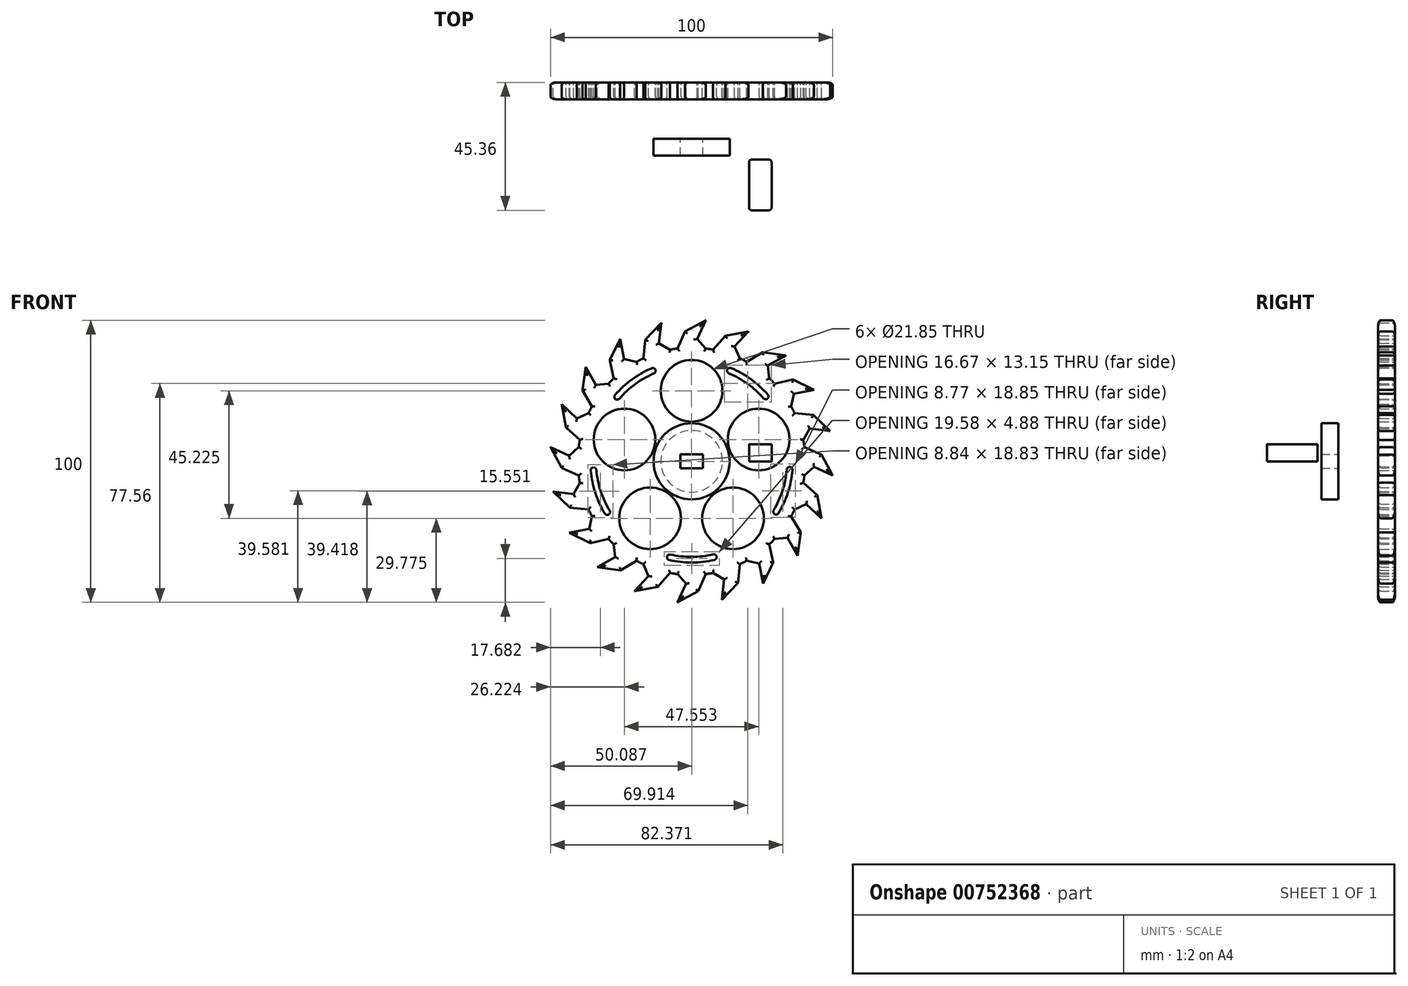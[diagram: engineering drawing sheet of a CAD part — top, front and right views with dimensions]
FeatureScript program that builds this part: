
annotation { "Feature Type Name" : "Feature", "Feature Type Description" : "" }
export const myFeature = defineFeature(function(context is Context, id is Id, definition is map)
    precondition{}
    {
        {
            var Q0;
            Q0=qCreatedBy(makeId("Front.planeOp"),FACE);
            var sketch = newSketch(context, id + "F0", { "sketchPlane" : qUnion([Q0])});
            skCircle(sketch, "E0", {"center": v(0, 0) * mm, "radius": 10.93 * mm});
            skLineSegment(sketch, "E1", {"start": v(0, 0) * mm, "end": v(0, 25) * mm, "construction": true});
            skCircle(sketch, "E2", {"center": v(0, 25) * mm, "radius": 10.43 * mm});
            skCircle(sketch, "E3.1.0", {"center": v(-23.78, 7.73) * mm, "radius": 10.43 * mm});
            skCircle(sketch, "E3.2.0", {"center": v(-14.7, -20.23) * mm, "radius": 10.43 * mm});
            skCircle(sketch, "E3.3.0", {"center": v(14.7, -20.23) * mm, "radius": 10.43 * mm});
            skCircle(sketch, "E3.4.0", {"center": v(23.78, 7.73) * mm, "radius": 10.43 * mm});
            skLineSegment(sketch, "E4.bottom", {"start": v(5, 40) * mm, "end": v(-5, 40) * mm, "construction": true});
            skPoint(sketch, "E4.middle", {"position": v(0, 45) * mm});
            skLineSegment(sketch, "E5", {"start": v(-5, 40) * mm, "end": v(-2.33, 46.08) * mm});
            skLineSegment(sketch, "E6", {"start": v(-2.33, 46.08) * mm, "end": v(5, 50) * mm});
            skLineSegment(sketch, "E7", {"start": v(5, 50) * mm, "end": v(1.93, 43.37) * mm});
            skLineSegment(sketch, "E8", {"start": v(1.93, 43.37) * mm, "end": v(5, 40) * mm});
            skLineSegment(sketch, "E9.1.0", {"start": v(-16.45, 43.1) * mm, "end": v(-10.7, 49.1) * mm});
            skLineSegment(sketch, "E9.1.1", {"start": v(-17.12, 36.5) * mm, "end": v(-16.45, 43.1) * mm});
            skLineSegment(sketch, "E9.1.2", {"start": v(-10.7, 49.1) * mm, "end": v(-11.57, 41.85) * mm});
            skPoint(sketch, "E9.1.3", {"position": v(-13.9, 42.8) * mm});
            skLineSegment(sketch, "E9.1.4", {"start": v(-7.6, 39.59) * mm, "end": v(-17.12, 36.5) * mm, "construction": true});
            skLineSegment(sketch, "E9.1.5", {"start": v(-11.57, 41.85) * mm, "end": v(-7.6, 39.59) * mm});
            skLineSegment(sketch, "E9.2.0", {"start": v(-28.97, 35.91) * mm, "end": v(-25.34, 43.39) * mm});
            skLineSegment(sketch, "E9.2.1", {"start": v(-27.56, 29.42) * mm, "end": v(-28.97, 35.91) * mm});
            skLineSegment(sketch, "E9.2.2", {"start": v(-25.34, 43.39) * mm, "end": v(-23.93, 36.22) * mm});
            skPoint(sketch, "E9.2.3", {"position": v(-26.45, 36.4) * mm});
            skLineSegment(sketch, "E9.2.4", {"start": v(-19.47, 35.3) * mm, "end": v(-27.56, 29.42) * mm, "construction": true});
            skLineSegment(sketch, "E9.2.5", {"start": v(-23.93, 36.22) * mm, "end": v(-19.47, 35.3) * mm});
            skLineSegment(sketch, "E9.3.0", {"start": v(-38.65, 25.2) * mm, "end": v(-37.51, 33.43) * mm});
            skLineSegment(sketch, "E9.3.1", {"start": v(-35.3, 19.47) * mm, "end": v(-38.65, 25.2) * mm});
            skLineSegment(sketch, "E9.3.2", {"start": v(-37.51, 33.43) * mm, "end": v(-33.96, 27.06) * mm});
            skPoint(sketch, "E9.3.3", {"position": v(-36.4, 26.45) * mm});
            skLineSegment(sketch, "E9.3.4", {"start": v(-29.42, 27.56) * mm, "end": v(-35.3, 19.47) * mm, "construction": true});
            skLineSegment(sketch, "E9.3.5", {"start": v(-33.96, 27.06) * mm, "end": v(-29.42, 27.56) * mm});
            skLineSegment(sketch, "E9.4.0", {"start": v(-44.54, 12.03) * mm, "end": v(-46, 20.2) * mm});
            skLineSegment(sketch, "E9.4.1", {"start": v(-39.59, 7.6) * mm, "end": v(-44.54, 12.03) * mm});
            skLineSegment(sketch, "E9.4.2", {"start": v(-46, 20.2) * mm, "end": v(-40.66, 15.24) * mm});
            skPoint(sketch, "E9.4.3", {"position": v(-42.8, 13.9) * mm});
            skLineSegment(sketch, "E9.4.4", {"start": v(-36.5, 17.12) * mm, "end": v(-39.59, 7.6) * mm, "construction": true});
            skLineSegment(sketch, "E9.4.5", {"start": v(-40.66, 15.24) * mm, "end": v(-36.5, 17.12) * mm});
            skLineSegment(sketch, "E9.5.0", {"start": v(-46.08, -2.33) * mm, "end": v(-50, 5) * mm});
            skLineSegment(sketch, "E9.5.1", {"start": v(-40, -5) * mm, "end": v(-46.08, -2.33) * mm});
            skLineSegment(sketch, "E9.5.2", {"start": v(-50, 5) * mm, "end": v(-43.37, 1.93) * mm});
            skPoint(sketch, "E9.5.3", {"position": v(-45, 0) * mm});
            skLineSegment(sketch, "E9.5.4", {"start": v(-40, 5) * mm, "end": v(-40, -5) * mm, "construction": true});
            skLineSegment(sketch, "E9.5.5", {"start": v(-43.37, 1.93) * mm, "end": v(-40, 5) * mm});
            skLineSegment(sketch, "E9.6.0", {"start": v(-43.1, -16.45) * mm, "end": v(-49.1, -10.7) * mm});
            skLineSegment(sketch, "E9.6.1", {"start": v(-36.5, -17.12) * mm, "end": v(-43.1, -16.45) * mm});
            skLineSegment(sketch, "E9.6.2", {"start": v(-49.1, -10.7) * mm, "end": v(-41.85, -11.57) * mm});
            skPoint(sketch, "E9.6.3", {"position": v(-42.8, -13.9) * mm});
            skLineSegment(sketch, "E9.6.4", {"start": v(-39.59, -7.6) * mm, "end": v(-36.5, -17.12) * mm, "construction": true});
            skLineSegment(sketch, "E9.6.5", {"start": v(-41.85, -11.57) * mm, "end": v(-39.59, -7.6) * mm});
            skLineSegment(sketch, "E9.7.0", {"start": v(-35.91, -28.97) * mm, "end": v(-43.39, -25.34) * mm});
            skLineSegment(sketch, "E9.7.1", {"start": v(-29.42, -27.56) * mm, "end": v(-35.91, -28.97) * mm});
            skLineSegment(sketch, "E9.7.2", {"start": v(-43.39, -25.34) * mm, "end": v(-36.22, -23.93) * mm});
            skPoint(sketch, "E9.7.3", {"position": v(-36.4, -26.45) * mm});
            skLineSegment(sketch, "E9.7.4", {"start": v(-35.3, -19.47) * mm, "end": v(-29.42, -27.56) * mm, "construction": true});
            skLineSegment(sketch, "E9.7.5", {"start": v(-36.22, -23.93) * mm, "end": v(-35.3, -19.47) * mm});
            skLineSegment(sketch, "E9.8.0", {"start": v(-25.2, -38.65) * mm, "end": v(-33.43, -37.51) * mm});
            skLineSegment(sketch, "E9.8.1", {"start": v(-19.47, -35.3) * mm, "end": v(-25.2, -38.65) * mm});
            skLineSegment(sketch, "E9.8.2", {"start": v(-33.43, -37.51) * mm, "end": v(-27.06, -33.96) * mm});
            skPoint(sketch, "E9.8.3", {"position": v(-26.45, -36.4) * mm});
            skLineSegment(sketch, "E9.8.4", {"start": v(-27.56, -29.42) * mm, "end": v(-19.47, -35.3) * mm, "construction": true});
            skLineSegment(sketch, "E9.8.5", {"start": v(-27.06, -33.96) * mm, "end": v(-27.56, -29.42) * mm});
            skLineSegment(sketch, "E9.9.0", {"start": v(-12.03, -44.54) * mm, "end": v(-20.2, -46) * mm});
            skLineSegment(sketch, "E9.9.1", {"start": v(-7.6, -39.59) * mm, "end": v(-12.03, -44.54) * mm});
            skLineSegment(sketch, "E9.9.2", {"start": v(-20.2, -46) * mm, "end": v(-15.24, -40.66) * mm});
            skPoint(sketch, "E9.9.3", {"position": v(-13.9, -42.8) * mm});
            skLineSegment(sketch, "E9.9.4", {"start": v(-17.12, -36.5) * mm, "end": v(-7.6, -39.59) * mm, "construction": true});
            skLineSegment(sketch, "E9.9.5", {"start": v(-15.24, -40.66) * mm, "end": v(-17.12, -36.5) * mm});
            skLineSegment(sketch, "E9.10.0", {"start": v(2.33, -46.08) * mm, "end": v(-5, -50) * mm});
            skLineSegment(sketch, "E9.10.1", {"start": v(5, -40) * mm, "end": v(2.33, -46.08) * mm});
            skLineSegment(sketch, "E9.10.2", {"start": v(-5, -50) * mm, "end": v(-1.93, -43.37) * mm});
            skPoint(sketch, "E9.10.3", {"position": v(0, -45) * mm});
            skLineSegment(sketch, "E9.10.4", {"start": v(-5, -40) * mm, "end": v(5, -40) * mm, "construction": true});
            skLineSegment(sketch, "E9.10.5", {"start": v(-1.93, -43.37) * mm, "end": v(-5, -40) * mm});
            skLineSegment(sketch, "E9.11.0", {"start": v(16.45, -43.1) * mm, "end": v(10.7, -49.1) * mm});
            skLineSegment(sketch, "E9.11.1", {"start": v(17.12, -36.5) * mm, "end": v(16.45, -43.1) * mm});
            skLineSegment(sketch, "E9.11.2", {"start": v(10.7, -49.1) * mm, "end": v(11.57, -41.85) * mm});
            skPoint(sketch, "E9.11.3", {"position": v(13.9, -42.8) * mm});
            skLineSegment(sketch, "E9.11.4", {"start": v(7.6, -39.59) * mm, "end": v(17.12, -36.5) * mm, "construction": true});
            skLineSegment(sketch, "E9.11.5", {"start": v(11.57, -41.85) * mm, "end": v(7.6, -39.59) * mm});
            skLineSegment(sketch, "E9.12.0", {"start": v(28.97, -35.91) * mm, "end": v(25.34, -43.39) * mm});
            skLineSegment(sketch, "E9.12.1", {"start": v(27.56, -29.42) * mm, "end": v(28.97, -35.91) * mm});
            skLineSegment(sketch, "E9.12.2", {"start": v(25.34, -43.39) * mm, "end": v(23.93, -36.22) * mm});
            skPoint(sketch, "E9.12.3", {"position": v(26.45, -36.4) * mm});
            skLineSegment(sketch, "E9.12.4", {"start": v(19.47, -35.3) * mm, "end": v(27.56, -29.42) * mm, "construction": true});
            skLineSegment(sketch, "E9.12.5", {"start": v(23.93, -36.22) * mm, "end": v(19.47, -35.3) * mm});
            skLineSegment(sketch, "E9.13.0", {"start": v(38.65, -25.2) * mm, "end": v(37.51, -33.43) * mm});
            skLineSegment(sketch, "E9.13.1", {"start": v(35.3, -19.47) * mm, "end": v(38.65, -25.2) * mm});
            skLineSegment(sketch, "E9.13.2", {"start": v(37.51, -33.43) * mm, "end": v(33.96, -27.06) * mm});
            skPoint(sketch, "E9.13.3", {"position": v(36.4, -26.45) * mm});
            skLineSegment(sketch, "E9.13.4", {"start": v(29.42, -27.56) * mm, "end": v(35.3, -19.47) * mm, "construction": true});
            skLineSegment(sketch, "E9.13.5", {"start": v(33.96, -27.06) * mm, "end": v(29.42, -27.56) * mm});
            skLineSegment(sketch, "E9.14.0", {"start": v(44.54, -12.03) * mm, "end": v(46, -20.2) * mm});
            skLineSegment(sketch, "E9.14.1", {"start": v(39.59, -7.6) * mm, "end": v(44.54, -12.03) * mm});
            skLineSegment(sketch, "E9.14.2", {"start": v(46, -20.2) * mm, "end": v(40.66, -15.24) * mm});
            skPoint(sketch, "E9.14.3", {"position": v(42.8, -13.9) * mm});
            skLineSegment(sketch, "E9.14.4", {"start": v(36.5, -17.12) * mm, "end": v(39.59, -7.6) * mm, "construction": true});
            skLineSegment(sketch, "E9.14.5", {"start": v(40.66, -15.24) * mm, "end": v(36.5, -17.12) * mm});
            skLineSegment(sketch, "E9.15.0", {"start": v(46.08, 2.33) * mm, "end": v(50, -5) * mm});
            skLineSegment(sketch, "E9.15.1", {"start": v(40, 5) * mm, "end": v(46.08, 2.33) * mm});
            skLineSegment(sketch, "E9.15.2", {"start": v(50, -5) * mm, "end": v(43.37, -1.93) * mm});
            skPoint(sketch, "E9.15.3", {"position": v(45, 0) * mm});
            skLineSegment(sketch, "E9.15.4", {"start": v(40, -5) * mm, "end": v(40, 5) * mm, "construction": true});
            skLineSegment(sketch, "E9.15.5", {"start": v(43.37, -1.93) * mm, "end": v(40, -5) * mm});
            skLineSegment(sketch, "E9.16.0", {"start": v(43.1, 16.45) * mm, "end": v(49.1, 10.7) * mm});
            skLineSegment(sketch, "E9.16.1", {"start": v(36.5, 17.12) * mm, "end": v(43.1, 16.45) * mm});
            skLineSegment(sketch, "E9.16.2", {"start": v(49.1, 10.7) * mm, "end": v(41.85, 11.57) * mm});
            skPoint(sketch, "E9.16.3", {"position": v(42.8, 13.9) * mm});
            skLineSegment(sketch, "E9.16.4", {"start": v(39.59, 7.6) * mm, "end": v(36.5, 17.12) * mm, "construction": true});
            skLineSegment(sketch, "E9.16.5", {"start": v(41.85, 11.57) * mm, "end": v(39.59, 7.6) * mm});
            skLineSegment(sketch, "E9.17.0", {"start": v(35.91, 28.97) * mm, "end": v(43.39, 25.34) * mm});
            skLineSegment(sketch, "E9.17.1", {"start": v(29.42, 27.56) * mm, "end": v(35.91, 28.97) * mm});
            skLineSegment(sketch, "E9.17.2", {"start": v(43.39, 25.34) * mm, "end": v(36.22, 23.93) * mm});
            skPoint(sketch, "E9.17.3", {"position": v(36.4, 26.45) * mm});
            skLineSegment(sketch, "E9.17.4", {"start": v(35.3, 19.47) * mm, "end": v(29.42, 27.56) * mm, "construction": true});
            skLineSegment(sketch, "E9.17.5", {"start": v(36.22, 23.93) * mm, "end": v(35.3, 19.47) * mm});
            skLineSegment(sketch, "E9.18.0", {"start": v(25.2, 38.65) * mm, "end": v(33.43, 37.51) * mm});
            skLineSegment(sketch, "E9.18.1", {"start": v(19.47, 35.3) * mm, "end": v(25.2, 38.65) * mm});
            skLineSegment(sketch, "E9.18.2", {"start": v(33.43, 37.51) * mm, "end": v(27.06, 33.96) * mm});
            skPoint(sketch, "E9.18.3", {"position": v(26.45, 36.4) * mm});
            skLineSegment(sketch, "E9.18.4", {"start": v(27.56, 29.42) * mm, "end": v(19.47, 35.3) * mm, "construction": true});
            skLineSegment(sketch, "E9.18.5", {"start": v(27.06, 33.96) * mm, "end": v(27.56, 29.42) * mm});
            skLineSegment(sketch, "E9.19.0", {"start": v(12.03, 44.54) * mm, "end": v(20.2, 46) * mm});
            skLineSegment(sketch, "E9.19.1", {"start": v(7.6, 39.59) * mm, "end": v(12.03, 44.54) * mm});
            skLineSegment(sketch, "E9.19.2", {"start": v(20.2, 46) * mm, "end": v(15.24, 40.66) * mm});
            skPoint(sketch, "E9.19.3", {"position": v(13.9, 42.8) * mm});
            skLineSegment(sketch, "E9.19.4", {"start": v(17.12, 36.5) * mm, "end": v(7.6, 39.59) * mm, "construction": true});
            skLineSegment(sketch, "E9.19.5", {"start": v(15.24, 40.66) * mm, "end": v(17.12, 36.5) * mm});
            skArc(sketch, "E10", {"start": v(-17.12, 36.5) * mm, "mid": v(-18.3, 35.92) * mm, "end": v(-19.47, 35.3) * mm});
            skArc(sketch, "E11.trimOffspring", {"start": v(-5, 40) * mm, "mid": v(-6.3, 39.81) * mm, "end": v(-7.6, 39.59) * mm});
            skArc(sketch, "E12.trimOffspring", {"start": v(7.6, 39.59) * mm, "mid": v(6.3, 39.81) * mm, "end": v(5, 40) * mm});
            skArc(sketch, "E13.trimOffspring", {"start": v(19.47, 35.3) * mm, "mid": v(18.3, 35.92) * mm, "end": v(17.12, 36.5) * mm});
            skArc(sketch, "E14.trimOffspring", {"start": v(29.42, 27.56) * mm, "mid": v(28.5, 28.5) * mm, "end": v(27.56, 29.42) * mm});
            skArc(sketch, "E15.trimOffspring", {"start": v(36.5, 17.12) * mm, "mid": v(35.92, 18.3) * mm, "end": v(35.3, 19.47) * mm});
            skArc(sketch, "E16.trimOffspring", {"start": v(40, 5) * mm, "mid": v(39.81, 6.3) * mm, "end": v(39.59, 7.6) * mm});
            skArc(sketch, "E17.trimOffspring", {"start": v(39.59, -7.6) * mm, "mid": v(39.81, -6.3) * mm, "end": v(40, -5) * mm});
            skArc(sketch, "E18.trimOffspring", {"start": v(35.3, -19.47) * mm, "mid": v(35.92, -18.3) * mm, "end": v(36.5, -17.12) * mm});
            skArc(sketch, "E19.trimOffspring", {"start": v(27.56, -29.42) * mm, "mid": v(28.5, -28.5) * mm, "end": v(29.42, -27.56) * mm});
            skArc(sketch, "E20.trimOffspring", {"start": v(17.12, -36.5) * mm, "mid": v(18.3, -35.92) * mm, "end": v(19.47, -35.3) * mm});
            skArc(sketch, "E21.trimOffspring", {"start": v(5, -40) * mm, "mid": v(6.3, -39.81) * mm, "end": v(7.6, -39.59) * mm});
            skArc(sketch, "E22.trimOffspring", {"start": v(-7.6, -39.59) * mm, "mid": v(-6.3, -39.81) * mm, "end": v(-5, -40) * mm});
            skArc(sketch, "E23.trimOffspring", {"start": v(-19.47, -35.3) * mm, "mid": v(-18.3, -35.92) * mm, "end": v(-17.12, -36.5) * mm});
            skArc(sketch, "E24.trimOffspring", {"start": v(-29.42, -27.56) * mm, "mid": v(-28.5, -28.5) * mm, "end": v(-27.56, -29.42) * mm});
            skArc(sketch, "E25.trimOffspring", {"start": v(-36.5, -17.12) * mm, "mid": v(-35.92, -18.3) * mm, "end": v(-35.3, -19.47) * mm});
            skArc(sketch, "E26.trimOffspring", {"start": v(-40, -5) * mm, "mid": v(-39.81, -6.3) * mm, "end": v(-39.59, -7.6) * mm});
            skArc(sketch, "E27.trimOffspring", {"start": v(-39.59, 7.6) * mm, "mid": v(-39.81, 6.3) * mm, "end": v(-40, 5) * mm});
            skArc(sketch, "E28.trimOffspring", {"start": v(-35.3, 19.47) * mm, "mid": v(-35.92, 18.3) * mm, "end": v(-36.5, 17.12) * mm});
            skArc(sketch, "E29.trimOffspring", {"start": v(-27.56, 29.42) * mm, "mid": v(-28.5, 28.5) * mm, "end": v(-29.42, 27.56) * mm});
            skArc(sketch, "E30.0", {"start": v(-13.74, 32.07) * mm, "mid": v(-20.58, 28.17) * mm, "end": v(-26.37, 22.85) * mm});
            skArc(sketch, "E31.0.startCap", {"start": v(-14.14, 32.99) * mm, "mid": v(-12.82, 32.46) * mm, "end": v(-13.35, 31.15) * mm});
            skArc(sketch, "E31.0.endCap", {"start": v(-25.61, 22.2) * mm, "mid": v(-27.02, 22.1) * mm, "end": v(-27.12, 23.5) * mm});
            skArc(sketch, "E31.0.left", {"start": v(-13.35, 31.15) * mm, "mid": v(-19.99, 27.37) * mm, "end": v(-25.61, 22.2) * mm});
            skArc(sketch, "E31.0.right", {"start": v(-14.14, 32.99) * mm, "mid": v(-21.17, 28.98) * mm, "end": v(-27.12, 23.5) * mm});
            skArc(sketch, "E32.1.0", {"start": v(-35.74, -3.25) * mm, "mid": v(-34.1, -11.18) * mm, "end": v(-30.73, -18.53) * mm});
            skArc(sketch, "E32.1.1", {"start": v(-29.02, -17.5) * mm, "mid": v(-29.36, -18.87) * mm, "end": v(-30.73, -18.53) * mm});
            skArc(sketch, "E32.1.2", {"start": v(-35.74, -3.25) * mm, "mid": v(-34.84, -2.16) * mm, "end": v(-33.75, -3.07) * mm});
            skArc(sketch, "E32.1.3", {"start": v(-34.75, -3.16) * mm, "mid": v(-33.15, -10.87) * mm, "end": v(-29.88, -18.02) * mm});
            skArc(sketch, "E32.1.4", {"start": v(-33.75, -3.07) * mm, "mid": v(-32.2, -10.55) * mm, "end": v(-29.02, -17.5) * mm});
            skArc(sketch, "E32.2.0", {"start": v(-7.95, -35) * mm, "mid": v(0.1, -35.89) * mm, "end": v(8.13, -34.96) * mm});
            skArc(sketch, "E32.2.1", {"start": v(7.68, -33) * mm, "mid": v(8.88, -33.76) * mm, "end": v(8.13, -34.96) * mm});
            skArc(sketch, "E32.2.2", {"start": v(-7.95, -35) * mm, "mid": v(-8.7, -33.8) * mm, "end": v(-7.51, -33.05) * mm});
            skArc(sketch, "E32.2.3", {"start": v(-7.73, -34.02) * mm, "mid": v(0.09, -34.89) * mm, "end": v(7.9, -33.98) * mm});
            skArc(sketch, "E32.2.4", {"start": v(-7.51, -33.05) * mm, "mid": v(0.09, -33.89) * mm, "end": v(7.68, -33) * mm});
            skArc(sketch, "E32.3.0", {"start": v(30.83, -18.38) * mm, "mid": v(34.16, -11) * mm, "end": v(35.76, -3.07) * mm});
            skArc(sketch, "E32.3.1", {"start": v(33.76, -2.9) * mm, "mid": v(34.85, -1.99) * mm, "end": v(35.76, -3.07) * mm});
            skArc(sketch, "E32.3.2", {"start": v(30.83, -18.38) * mm, "mid": v(29.45, -18.73) * mm, "end": v(29.1, -17.35) * mm});
            skArc(sketch, "E32.3.3", {"start": v(29.97, -17.87) * mm, "mid": v(33.2, -10.7) * mm, "end": v(34.76, -2.98) * mm});
            skArc(sketch, "E32.3.4", {"start": v(29.1, -17.35) * mm, "mid": v(32.26, -10.4) * mm, "end": v(33.76, -2.9) * mm});
            skArc(sketch, "E32.4.0", {"start": v(27, 23.64) * mm, "mid": v(21.02, 29.09) * mm, "end": v(13.97, 33.06) * mm});
            skArc(sketch, "E32.4.1", {"start": v(13.2, 31.22) * mm, "mid": v(12.66, 32.53) * mm, "end": v(13.97, 33.06) * mm});
            skArc(sketch, "E32.4.2", {"start": v(27, 23.64) * mm, "mid": v(26.91, 22.23) * mm, "end": v(25.5, 22.32) * mm});
            skArc(sketch, "E32.4.3", {"start": v(26.25, 22.98) * mm, "mid": v(20.44, 28.28) * mm, "end": v(13.58, 32.14) * mm});
            skArc(sketch, "E32.4.4", {"start": v(25.5, 22.32) * mm, "mid": v(19.85, 27.47) * mm, "end": v(13.2, 31.22) * mm});
            skLineSegment(sketch, "E33", {"start": v(0, 45) * mm, "end": v(0, 0) * mm, "construction": true});
            skCircle(sketch, "E34", {"center": v(0, 25) * mm, "radius": 10.93 * mm});
            skCircle(sketch, "E35.1.0", {"center": v(-23.78, 7.73) * mm, "radius": 10.93 * mm});
            skCircle(sketch, "E35.2.0", {"center": v(-14.7, -20.23) * mm, "radius": 10.93 * mm});
            skCircle(sketch, "E35.3.0", {"center": v(14.7, -20.23) * mm, "radius": 10.93 * mm});
            skCircle(sketch, "E35.4.0", {"center": v(23.78, 7.73) * mm, "radius": 10.93 * mm});
            skSolve(sketch);
        }
        {
            var Q0;
            Q0=makeQuery(id+"F0.imprint","IMPRINT",FACE,{"disambiguationData":[TD([[makeQuery(id+"F0.imprint","IMPRINT",EDGE,{"derivedFrom":sQuery(id+"F0.wireOp",EDGE,"E0")}),-1.0]])]});
            extrude(context, id + "F1", {"entities" : qUnion([Q0]), "depth" : 6 * mm, "offsetDistance" : 25 * mm});
        }
        {
            var Q0;
            Q0=makeQuery(id+"F1.opExtrude","CAP_FACE",FACE,{"disambiguationData":[OSD([sQuery(id+"F0.wireOp",EDGE,"E0"),sQuery(id+"F0.wireOp",EDGE,"E2"),sQuery(id+"F0.wireOp",EDGE,"E3.1.0"),sQuery(id+"F0.wireOp",EDGE,"E3.2.0"),sQuery(id+"F0.wireOp",EDGE,"E3.3.0"),sQuery(id+"F0.wireOp",EDGE,"E3.4.0"),sQuery(id+"F0.wireOp",EDGE,"6w4LuyIg-Judz-7qcx-iNhM-kCVs0XRHMAQz.left"),sQuery(id+"F0.wireOp",EDGE,"6w4LuyIg-Judz-7qcx-iNhM-kCVs0XRHMAQz.right"),sQuery(id+"F0.wireOp",EDGE,"GuxD1Two-tXSI-jhGi-diOq-QsG6SmieNdRW"),sQuery(id+"F0.wireOp",EDGE,"9e989a9f-be13-4d0f-822f-95c7c0624428.1.0"),sQuery(id+"F0.wireOp",EDGE,"9e989a9f-be13-4d0f-822f-95c7c0624428.1.1"),sQuery(id+"F0.wireOp",EDGE,"9e989a9f-be13-4d0f-822f-95c7c0624428.1.2"),sQuery(id+"F0.wireOp",EDGE,"9e989a9f-be13-4d0f-822f-95c7c0624428.2.0"),sQuery(id+"F0.wireOp",EDGE,"9e989a9f-be13-4d0f-822f-95c7c0624428.2.1"),sQuery(id+"F0.wireOp",EDGE,"9e989a9f-be13-4d0f-822f-95c7c0624428.2.2"),sQuery(id+"F0.wireOp",EDGE,"9e989a9f-be13-4d0f-822f-95c7c0624428.3.0"),sQuery(id+"F0.wireOp",EDGE,"9e989a9f-be13-4d0f-822f-95c7c0624428.3.1"),sQuery(id+"F0.wireOp",EDGE,"9e989a9f-be13-4d0f-822f-95c7c0624428.3.2"),sQuery(id+"F0.wireOp",EDGE,"9e989a9f-be13-4d0f-822f-95c7c0624428.4.0"),sQuery(id+"F0.wireOp",EDGE,"9e989a9f-be13-4d0f-822f-95c7c0624428.4.1"),sQuery(id+"F0.wireOp",EDGE,"9e989a9f-be13-4d0f-822f-95c7c0624428.4.2"),sQuery(id+"F0.wireOp",EDGE,"486a15bc-75c9-41d0-808c-e5c4775e6e80.filletArc"),sQuery(id+"F0.wireOp",EDGE,"d314a861-2769-46d2-9bec-117903992242.filletArc"),sQuery(id+"F0.wireOp",EDGE,"5d220be9-c9be-4508-b7a3-f434c5fdea58.filletArc"),sQuery(id+"F0.wireOp",EDGE,"2974d6c2-e4a2-45df-9bc2-224e587c2884.filletArc"),sQuery(id+"F0.wireOp",EDGE,"3265ed39-f9f2-4246-9e43-8a9d8c4dec78.filletArc")])],"isStart":false});
            var Q1;
            Q1=makeQuery(id+"F1.opExtrude","CAP_FACE",FACE,{"disambiguationData":[OSD([sQuery(id+"F0.wireOp",EDGE,"E0"),sQuery(id+"F0.wireOp",EDGE,"E2"),sQuery(id+"F0.wireOp",EDGE,"E3.1.0"),sQuery(id+"F0.wireOp",EDGE,"E3.2.0"),sQuery(id+"F0.wireOp",EDGE,"E3.3.0"),sQuery(id+"F0.wireOp",EDGE,"E3.4.0"),sQuery(id+"F0.wireOp",EDGE,"6w4LuyIg-Judz-7qcx-iNhM-kCVs0XRHMAQz.left"),sQuery(id+"F0.wireOp",EDGE,"6w4LuyIg-Judz-7qcx-iNhM-kCVs0XRHMAQz.right"),sQuery(id+"F0.wireOp",EDGE,"GuxD1Two-tXSI-jhGi-diOq-QsG6SmieNdRW"),sQuery(id+"F0.wireOp",EDGE,"9e989a9f-be13-4d0f-822f-95c7c0624428.1.0"),sQuery(id+"F0.wireOp",EDGE,"9e989a9f-be13-4d0f-822f-95c7c0624428.1.1"),sQuery(id+"F0.wireOp",EDGE,"9e989a9f-be13-4d0f-822f-95c7c0624428.1.2"),sQuery(id+"F0.wireOp",EDGE,"9e989a9f-be13-4d0f-822f-95c7c0624428.2.0"),sQuery(id+"F0.wireOp",EDGE,"9e989a9f-be13-4d0f-822f-95c7c0624428.2.1"),sQuery(id+"F0.wireOp",EDGE,"9e989a9f-be13-4d0f-822f-95c7c0624428.2.2"),sQuery(id+"F0.wireOp",EDGE,"9e989a9f-be13-4d0f-822f-95c7c0624428.3.0"),sQuery(id+"F0.wireOp",EDGE,"9e989a9f-be13-4d0f-822f-95c7c0624428.3.1"),sQuery(id+"F0.wireOp",EDGE,"9e989a9f-be13-4d0f-822f-95c7c0624428.3.2"),sQuery(id+"F0.wireOp",EDGE,"9e989a9f-be13-4d0f-822f-95c7c0624428.4.0"),sQuery(id+"F0.wireOp",EDGE,"9e989a9f-be13-4d0f-822f-95c7c0624428.4.1"),sQuery(id+"F0.wireOp",EDGE,"9e989a9f-be13-4d0f-822f-95c7c0624428.4.2"),sQuery(id+"F0.wireOp",EDGE,"486a15bc-75c9-41d0-808c-e5c4775e6e80.filletArc"),sQuery(id+"F0.wireOp",EDGE,"d314a861-2769-46d2-9bec-117903992242.filletArc"),sQuery(id+"F0.wireOp",EDGE,"5d220be9-c9be-4508-b7a3-f434c5fdea58.filletArc"),sQuery(id+"F0.wireOp",EDGE,"2974d6c2-e4a2-45df-9bc2-224e587c2884.filletArc"),sQuery(id+"F0.wireOp",EDGE,"3265ed39-f9f2-4246-9e43-8a9d8c4dec78.filletArc")])],"isStart":true});
            fillet(context, id + "F2", {"entities" : qUnion([Q0, Q1]), "radius" : 1 * mm, "tangentPropagation" : true, "allowEdgeOverflow" : false});
        }
        {
            var Q0;
            Q0=qCreatedBy(makeId("Top.planeOp"),FACE);
            var sketch = newSketch(context, id + "F3", { "sketchPlane" : qUnion([Q0])});
            skLineSegment(sketch, "E36.bottom", {"start": v(21.35, -27.36) * mm, "end": v(27.35, -27.36) * mm});
            skLineSegment(sketch, "E36.top", {"start": v(21.35, -45.36) * mm, "end": v(27.35, -45.36) * mm});
            skLineSegment(sketch, "E36.left", {"start": v(20.35, -28.36) * mm, "end": v(20.35, -44.36) * mm});
            skLineSegment(sketch, "E36.right", {"start": v(28.35, -28.36) * mm, "end": v(28.35, -44.36) * mm});
            skPoint(sketch, "E36.middle", {"position": v(24.35, -36.36) * mm});
            skPoint(sketch, "E37.visualSharp", {"position": v(20.35, -45.36) * mm});
            skArc(sketch, "E37.filletArc", {"start": v(20.35, -44.36) * mm, "mid": v(20.64, -45.06) * mm, "end": v(21.35, -45.36) * mm});
            skPoint(sketch, "E38.visualSharp", {"position": v(28.35, -45.36) * mm});
            skArc(sketch, "E38.filletArc", {"start": v(27.35, -45.36) * mm, "mid": v(28.05, -45.06) * mm, "end": v(28.35, -44.36) * mm});
            skPoint(sketch, "E39.visualSharp", {"position": v(28.35, -27.36) * mm});
            skArc(sketch, "E39.filletArc", {"start": v(28.35, -28.36) * mm, "mid": v(28.05, -27.65) * mm, "end": v(27.35, -27.36) * mm});
            skPoint(sketch, "E40.visualSharp", {"position": v(20.35, -27.36) * mm});
            skArc(sketch, "E40.filletArc", {"start": v(21.35, -27.36) * mm, "mid": v(20.64, -27.65) * mm, "end": v(20.35, -28.36) * mm});
            skSolve(sketch);
        }
        {
            var Q0;
            Q0=makeQuery(id+"F3.imprint","IMPRINT",FACE,{"disambiguationData":[TD([[makeQuery(id+"F3.imprint","IMPRINT",EDGE,{"derivedFrom":sQuery(id+"F3.wireOp",EDGE,"E36.bottom")}),-1.0]])]});
            extrude(context, id + "F4", {"entities" : qUnion([Q0]), "depth" : 6 * mm, "offsetDistance" : 25 * mm});
        }
        {
            var Q0;
            Q0=qCreatedBy(makeId("Front.planeOp"),FACE);
            var sketch = newSketch(context, id + "F5", { "sketchPlane" : qUnion([Q0])});
            skCircle(sketch, "E41", {"center": v(0, 0) * mm, "radius": 13.5 * mm});
            skLineSegment(sketch, "E42.bottom", {"start": v(4, -2.5) * mm, "end": v(-4, -2.5) * mm});
            skLineSegment(sketch, "E42.top", {"start": v(4, 2.5) * mm, "end": v(-4, 2.5) * mm});
            skLineSegment(sketch, "E42.left", {"start": v(4, -2.5) * mm, "end": v(4, 2.5) * mm});
            skLineSegment(sketch, "E42.right", {"start": v(-4, -2.5) * mm, "end": v(-4, 2.5) * mm});
            skSolve(sketch);
        }
        {
            var Q0;
            Q0=qSketchRegion(id+"F5",true);
            extrude(context, id + "F6", {"entities" : qUnion([Q0]), "depth" : 26 * mm, "offsetDistance" : 25 * mm, "hasSecondDirection" : true, "secondDirectionOppositeDirection" : false, "secondDirectionDepth" : 20 * mm});
        }
    });
